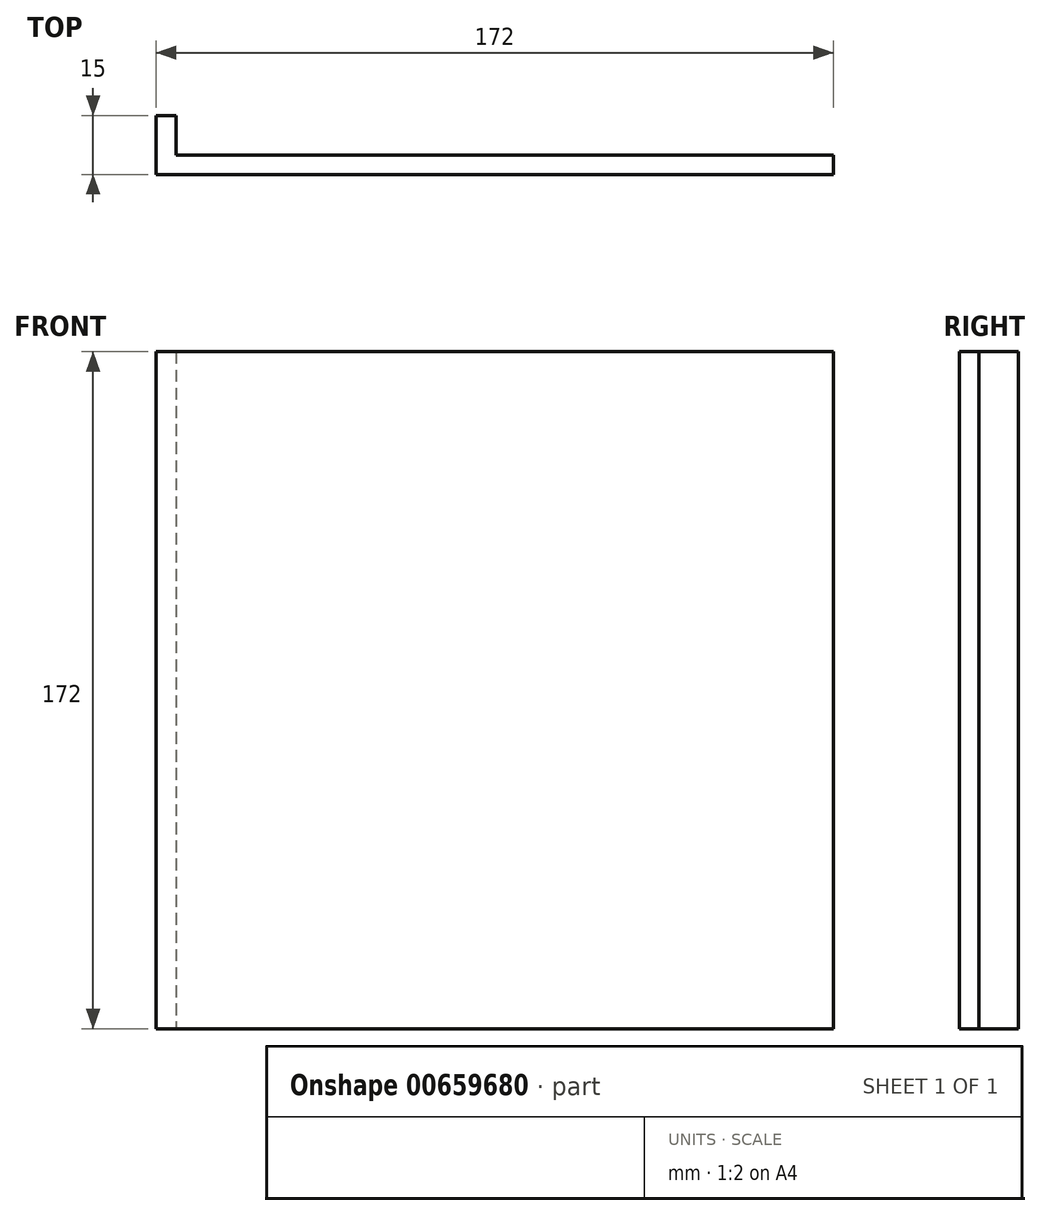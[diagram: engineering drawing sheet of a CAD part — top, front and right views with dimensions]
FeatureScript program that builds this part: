
annotation { "Feature Type Name" : "Feature", "Feature Type Description" : "" }
export const myFeature = defineFeature(function(context is Context, id is Id, definition is map)
    precondition{}
    {
        {
            var Q0;
            Q0=qCreatedBy(makeId("Front.planeOp"),FACE);
            var sketch = newSketch(context, id + "F0", { "sketchPlane" : qUnion([Q0])});
            skLineSegment(sketch, "E0.bottom", {"start": v(-86, 0) * mm, "end": v(86, 0) * mm});
            skLineSegment(sketch, "E0.top", {"start": v(-86, -172) * mm, "end": v(86, -172) * mm});
            skLineSegment(sketch, "E0.left", {"start": v(-86, 0) * mm, "end": v(-86, -172) * mm});
            skLineSegment(sketch, "E0.right", {"start": v(86, 0) * mm, "end": v(86, -172) * mm});
            skSolve(sketch);
        }
        {
            var Q0;
            Q0=makeQuery(id+"F0.imprint","IMPRINT",FACE,{"disambiguationData":[TD([[makeQuery(id+"F0.imprint","IMPRINT",EDGE,{"derivedFrom":sQuery(id+"F0.wireOp",EDGE,"E0.bottom")}),-1.0]])]});
            extrude(context, id + "F1", {"entities" : qUnion([Q0]), "depth" : 5 * mm, "offsetDistance" : 25 * mm});
        }
        {
            var Q0;
            Q0=makeQuery(id+"F1.opExtrude","SWEPT_FACE",FACE,{"disambiguationData":[OSD([sQuery(id+"F0.wireOp",EDGE,"E0.left")])]});
            var sketch = newSketch(context, id + "F2", { "sketchPlane" : qUnion([Q0])});
            skLineSegment(sketch, "E1.bottom", {"start": v(5, -172) * mm, "end": v(-10, -172) * mm});
            skLineSegment(sketch, "E1.top", {"start": v(5, 0) * mm, "end": v(-10, 0) * mm});
            skLineSegment(sketch, "E1.left", {"start": v(5, -172) * mm, "end": v(5, 0) * mm});
            skLineSegment(sketch, "E1.right", {"start": v(-10, -172) * mm, "end": v(-10, 0) * mm});
            skSolve(sketch);
        }
        {
            var Q0;
            Q0 = qSketchRegion(id + "F2", true);
            extrude(context, id + "F3", {"entities" : qUnion([Q0]), "operationType" : NewBodyOperationType.ADD, "oppositeDirection" : true, "depth" : 5 * mm, "offsetDistance" : 25 * mm});
        }
    });
